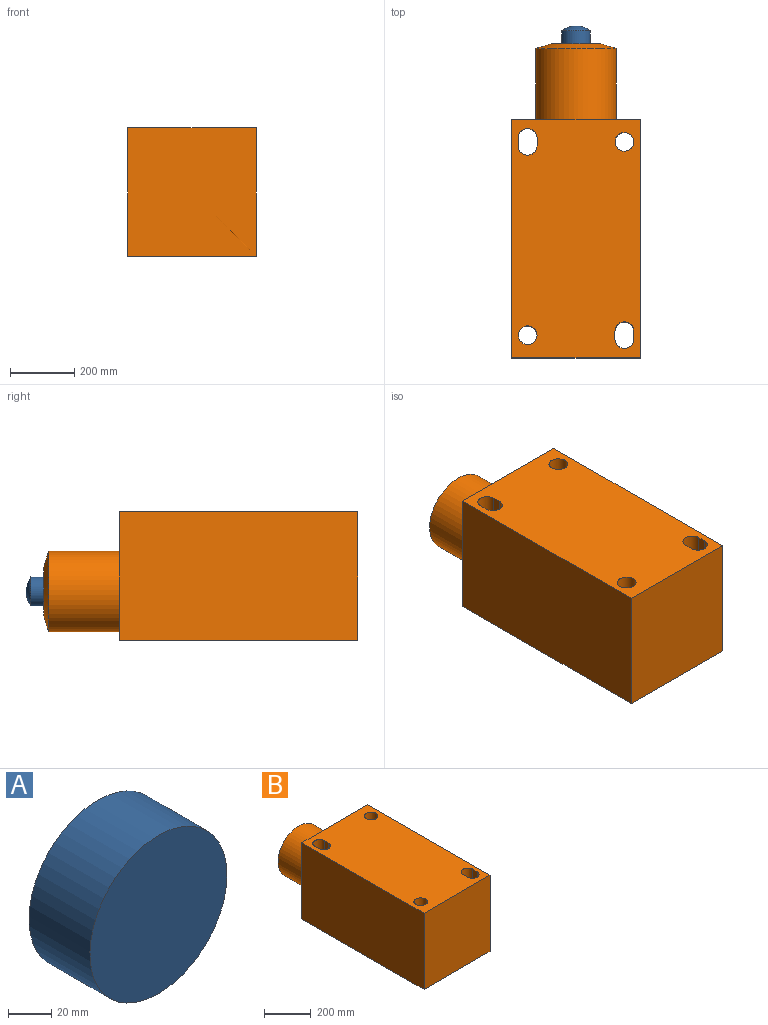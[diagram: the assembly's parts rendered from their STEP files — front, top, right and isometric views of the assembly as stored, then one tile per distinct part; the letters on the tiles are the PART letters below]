
ASSEMBLY  parts=2 mates=1
PART A: 3 faces, bbox 90x55x90 mm
  f0: plane 90x90mm, normal (0,-1,0), area 6361.7mm2, adj f1
  f1: cylinder r=45mm len=90mm, axis (0,-1,0), area 11309.7mm2, adj f0,f2
  f2: sphere r=75mm, area 7068.6mm2, adj f1
PART B: 19 faces, bbox 400x975x400 mm
  f0: plane 740x400mm, normal (0,0,1), area 282531.7mm2, adj f2,f3,f4,f5,f6,f7,f8,f9
  f1: plane 740x400mm, normal (0,0,-1), area 282531.7mm2, adj f2,f3,f4,f5,f6,f7,f8,f9
  f2: plane 400x400mm, normal (0,-1,0), area 160000mm2, adj f0,f1,f3,f5
  f3: plane 740x400mm, normal (1,0,0), area 296000mm2, adj f0,f1,f2,f4
  f4: plane 400x400mm, normal (0,1,0), area 110912.6mm2, adj f0,f1,f3,f5,f16
  f5: plane 740x400mm, normal (-1,0,0), area 296000mm2, adj f0,f1,f2,f4
  f6: plane 400x25mm, normal (-1,0,0), area 10000mm2, adj f0,f1,f7,f9
  f7: cylinder r=29mm len=400mm, axis (0,0,1), area 36442.5mm2, adj f0,f1,f6,f8
  f8: plane 400x25mm, normal (1,0,0), area 10000mm2, adj f0,f1,f7,f9
  f9: cylinder r=29mm len=400mm, axis (0,0,1), area 36442.5mm2, adj f0,f1,f6,f8
  f10: plane 400x25mm, normal (-1,0,0), area 10000mm2, adj f0,f1,f11,f13
  f11: cylinder r=29mm len=400mm, axis (0,0,1), area 36442.5mm2, adj f0,f1,f10,f12
  f12: plane 400x25mm, normal (1,0,0), area 10000mm2, adj f0,f1,f11,f13
  f13: cylinder r=29mm len=400mm, axis (0,0,1), area 36442.5mm2, adj f0,f1,f10,f12
  f14: cylinder r=29mm len=400mm, axis (0,0,1), area 72884.9mm2, adj f0,f1
  f15: cylinder r=29mm len=400mm, axis (0,0,1), area 72884.9mm2, adj f0,f1
  f16: cylinder r=125mm len=250mm, axis (0,-1,0), area 172787.6mm2, adj f4,f17
  f17: cone r=75mm half-angle=73.3deg, axis (0,-1,0), area 32799.2mm2, adj f16,f18
  f18: plane 150x150mm, normal (0,1,0), area 17671.5mm2, adj f17
PLACE A t=(-524.09,-129.67,6.18)mm
PLACE B t=(-524.09,-129.67,6.18)mm
MATE fastened B.f16 <-> A.f1  axis (0,1,0) through (-524.09,475.33,158.18)mm
